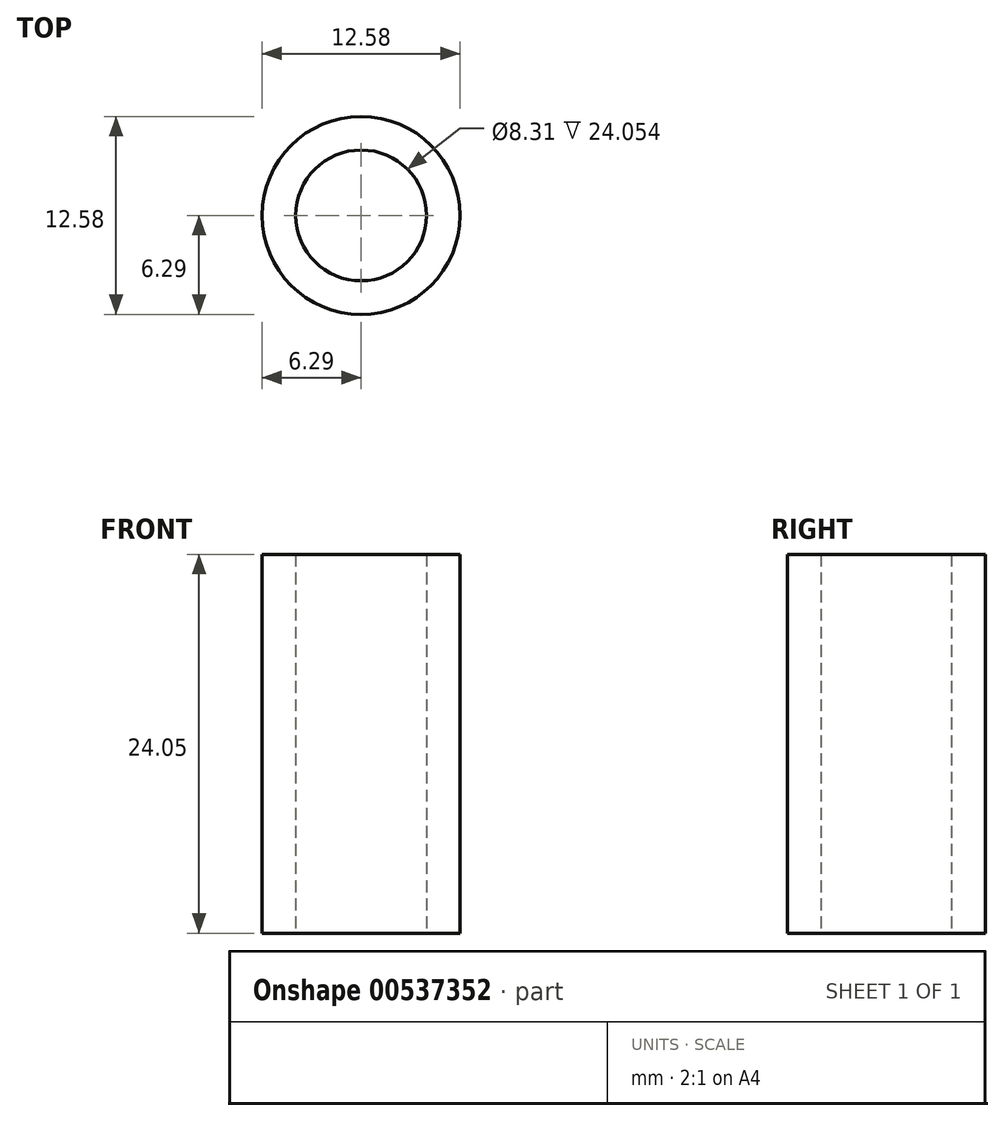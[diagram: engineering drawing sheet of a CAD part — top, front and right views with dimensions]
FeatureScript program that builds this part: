
annotation { "Feature Type Name" : "Feature", "Feature Type Description" : "" }
export const myFeature = defineFeature(function(context is Context, id is Id, definition is map)
    precondition{}
    {
        {
            var Q0;
            Q0=qCreatedBy(makeId("Top.planeOp"),FACE);
            var sketch = newSketch(context, id + "F0", { "sketchPlane" : qUnion([Q0])});
            skCircle(sketch, "E0", {"center": v(0, 0) * mm, "radius": 4.15 * mm});
            skCircle(sketch, "E1", {"center": v(0, 0) * mm, "radius": 6.29 * mm});
            skSolve(sketch);
        }
        {
            var Q0;
            Q0=makeQuery(id+"F0.imprint","IMPRINT",FACE,{"disambiguationData":[TD([[makeQuery(id+"F0.imprint","IMPRINT",EDGE,{"derivedFrom":sQuery(id+"F0.wireOp",EDGE,"E0")}),-1.0]])]});
            extrude(context, id + "F1", {"entities" : qUnion([Q0]), "depth" : 24.05 * mm, "offsetDistance" : 25.4 * mm});
        }
    });
